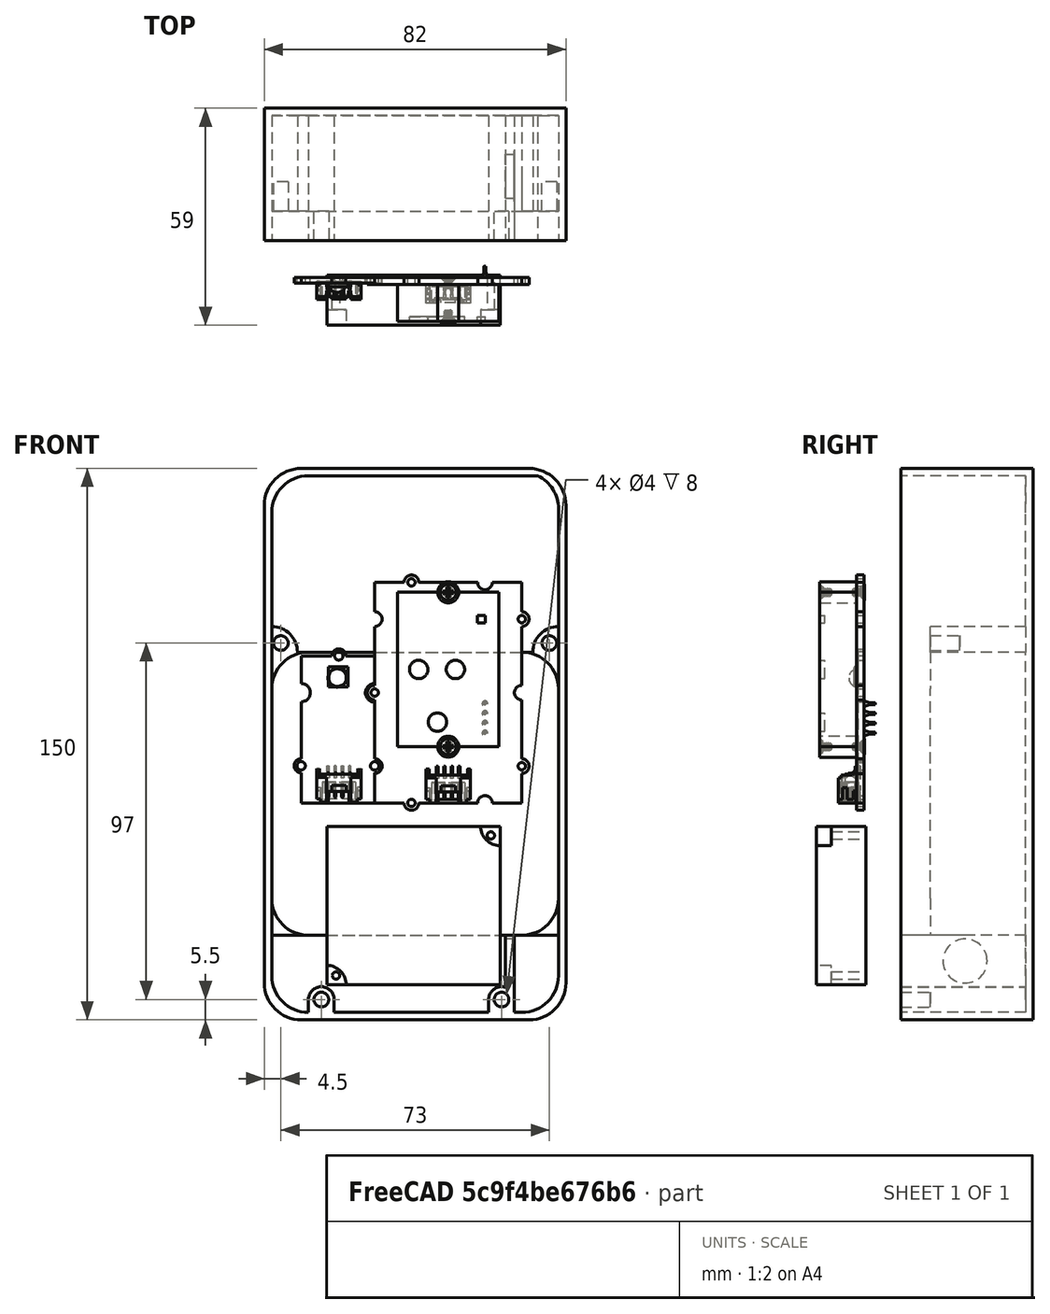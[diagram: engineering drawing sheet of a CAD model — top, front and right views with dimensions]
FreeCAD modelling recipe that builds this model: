
FCSTD DOCUMENT  (FreeCAD 0.20R29177 +233 (Git))
Label: wearableCad_09_10_2022
License: All rights reserved
LicenseURL: http://en.wikipedia.org/wiki/All_rights_reserved
objects: Part::Cylinder×30, Part::Box×23, Part::Cut×23, Part::MultiFuse×14, Part::Feature×3
note: 93 computed .brp shape members not serialized (recipe doc carries the construction recipe); baked Part::Feature solids carry a one-line shape summary decoded from their .brp

FEATURE [Part::Feature] Feature  label="Odroid-C4"
  Placement = pos=(66,-10,0) rot=(0.57735,-0.57735,0.57735;2.0944rad)
  shape: bbox 57.1 x 20.65 x 89.5 mm, 2775 faces, 0 solids (baked)
FEATURE [Part::Feature] Feature001  label="SCD30"
  Placement = pos=(-1.3e-14,-22,57) rot=(0,-1,0;1.5708rad)
  shape: bbox 44 x 15.1 x 64 mm, 422 faces, 13 solids (baked)
FEATURE [Part::Feature] Feature002  label="bme280"
  Placement = pos=(-60,-20,58) rot=(0.707107,0,0.707107;3.14159rad)
  shape: bbox 23.8 x 6.016 x 41.9 mm, 221 faces, 2 solids (baked)
FEATURE [Part::MultiFuse] Fusion  label="i2cSensors"
  Placement = pos=(68,0,0) rot=(0,0,1;0rad)
  Shapes = -> [Feature001,Feature002]
FEATURE [Part::Box] Box  label="ips7100"
  AttacherType = Attacher::AttachEngine3D
  Height = 43.1
  Length = 47.1
  Width = 13.55
FEATURE [Part::Cylinder] Cylinder
  Angle = 360
  AttacherType = Attacher::AttachEngine3D
  FirstAngle = 0
  Height = 13.55
  Placement = pos=(2.5,13.55,2.5) rot=(1,0,0;1.5708rad)
  Radius = 1
  SecondAngle = 0
FEATURE [Part::Cylinder] Cylinder001  label="semiCut"
  Angle = 90
  AttacherType = Attacher::AttachEngine3D
  FirstAngle = 0
  Height = 4.13
  Placement = pos=(0,4.13,-9e-16) rot=(1,0,0;1.5708rad)
  Radius = 5.25
  SecondAngle = 0
FEATURE [Part::MultiFuse] Fusion001  label="ipsCut"
  Shapes = -> [Cylinder,Cylinder001]
FEATURE [Part::Cylinder] Cylinder002
  Angle = 360
  AttacherType = Attacher::AttachEngine3D
  FirstAngle = 0
  Height = 13.55
  Placement = pos=(2.5,13.55,2.5) rot=(1,0,0;1.5708rad)
  Radius = 1
  SecondAngle = 0
FEATURE [Part::Cylinder] Cylinder003  label="semiCut001"
  Angle = 90
  AttacherType = Attacher::AttachEngine3D
  FirstAngle = 0
  Height = 4.13
  Placement = pos=(0,4.13,-9e-16) rot=(1,0,0;1.5708rad)
  Radius = 5.25
  SecondAngle = 0
FEATURE [Part::MultiFuse] Fusion002  label="ipsCut001"
  Placement = pos=(47.1,0,43.1) rot=(0,1,0;3.14159rad)
  Shapes = -> [Cylinder002,Cylinder003]
FEATURE [Part::MultiFuse] Fusion003
  Shapes = -> [Fusion001,Fusion002]
FEATURE [Part::Cut] Cut  label="ips7100V"
  Base = -> Box
  Placement = pos=(15,-33,7.55) rot=(0,0,1;0rad)
  Tool = -> Fusion003
FEATURE [Part::Box] Box001  label="V25B"
  AttacherType = Attacher::AttachEngine3D
  Height = 77
  Length = 78
  Width = 26
FEATURE [Part::Cylinder] Cylinder004
  Angle = 90
  AttacherType = Attacher::AttachEngine3D
  FirstAngle = 0
  Height = 26
  Placement = pos=(0,26,-5.8e-15) rot=(1,0,0;1.5708rad)
  Radius = 10
  SecondAngle = 0
FEATURE [Part::Box] Box002  label="Cube"
  AttacherType = Attacher::AttachEngine3D
  Height = 10
  Length = 10
  Width = 26
FEATURE [Part::Cut] Cut001
  Base = -> Box002
  Placement = pos=(68,0,67) rot=(0,0,1;0rad)
  Tool = -> Cylinder004
FEATURE [Part::Box] Box003  label="Cube001"
  AttacherType = Attacher::AttachEngine3D
  Height = 10
  Length = 10
  Width = 26
FEATURE [Part::Cylinder] Cylinder005
  Angle = 90
  AttacherType = Attacher::AttachEngine3D
  FirstAngle = 0
  Height = 26
  Placement = pos=(0,26,-5.8e-15) rot=(1,0,0;1.5708rad)
  Radius = 10
  SecondAngle = 0
FEATURE [Part::Cut] Cut002
  Base = -> Box003
  Placement = pos=(68,0,10) rot=(0,1,0;1.5708rad)
  Tool = -> Cylinder005
FEATURE [Part::Box] Box004  label="Cube002"
  AttacherType = Attacher::AttachEngine3D
  Height = 10
  Length = 10
  Width = 26
FEATURE [Part::Cylinder] Cylinder006
  Angle = 90
  AttacherType = Attacher::AttachEngine3D
  FirstAngle = 0
  Height = 26
  Placement = pos=(0,26,-5.8e-15) rot=(1,0,0;1.5708rad)
  Radius = 10
  SecondAngle = 0
FEATURE [Part::Cut] Cut003
  Base = -> Box004
  Placement = pos=(10,0,10) rot=(0,1,0;3.14159rad)
  Tool = -> Cylinder006
FEATURE [Part::Box] Box005  label="Cube003"
  AttacherType = Attacher::AttachEngine3D
  Height = 10
  Length = 10
  Width = 26
FEATURE [Part::Cylinder] Cylinder007
  Angle = 90
  AttacherType = Attacher::AttachEngine3D
  FirstAngle = 0
  Height = 26
  Placement = pos=(0,26,-5.8e-15) rot=(1,0,0;1.5708rad)
  Radius = 10
  SecondAngle = 0
FEATURE [Part::Cut] Cut004
  Base = -> Box005
  Placement = pos=(10,0,67) rot=(0,-1,0;1.5708rad)
  Tool = -> Cylinder007
FEATURE [Part::MultiFuse] Fusion004  label="v25Cuts"
  Shapes = -> [Cut001,Cut002,Cut003,Cut004]
FEATURE [Part::Cut] Cut005  label="V25B001"
  Base = -> Box001
  Placement = pos=(0,-2,21) rot=(0,0,1;0rad)
  Tool = -> Fusion004
FEATURE [Part::Box] Box007  label="Cube004"
  AttacherType = Attacher::AttachEngine3D
  Height = 10
  Length = 10
  Placement = pos=(0,-10,0) rot=(0,0,1;0rad)
  Width = 36
FEATURE [Part::Cylinder] Cylinder008
  Angle = 90
  AttacherType = Attacher::AttachEngine3D
  FirstAngle = 0
  Height = 36
  Placement = pos=(0,26,-5.8e-15) rot=(1,0,0;1.5708rad)
  Radius = 10
  SecondAngle = 0
FEATURE [Part::Cut] Cut006
  Base = -> Box007
  Placement = pos=(8,18,8) rot=(-0.707107,0,0.707107;3.14159rad)
  Tool = -> Cylinder008
FEATURE [Part::Box] Box008  label="baseOut001"
  AttacherType = Attacher::AttachEngine3D
  Height = 150
  Length = 82
  Placement = pos=(80,26,-2) rot=(0,0,1;3.14159rad)
  Width = 36
FEATURE [Part::Box] Box009  label="Cube005"
  AttacherType = Attacher::AttachEngine3D
  Height = 10
  Length = 10
  Placement = pos=(0,-10,0) rot=(0,0,1;0rad)
  Width = 36
FEATURE [Part::Cylinder] Cylinder009
  Angle = 90
  AttacherType = Attacher::AttachEngine3D
  FirstAngle = 0
  Height = 36
  Placement = pos=(0,26,-5.8e-15) rot=(1,0,0;1.5708rad)
  Radius = 10
  SecondAngle = 0
FEATURE [Part::Cut] Cut007
  Base = -> Box009
  Placement = pos=(70,18,8) rot=(1,0,0;3.14159rad)
  Tool = -> Cylinder009
FEATURE [Part::Box] Box010  label="Cube006"
  AttacherType = Attacher::AttachEngine3D
  Height = 10
  Length = 10
  Placement = pos=(0,-10,0) rot=(0,0,1;0rad)
  Width = 36
FEATURE [Part::Cylinder] Cylinder010
  Angle = 90
  AttacherType = Attacher::AttachEngine3D
  FirstAngle = 0
  Height = 36
  Placement = pos=(0,26,-5.8e-15) rot=(1,0,0;1.5708rad)
  Radius = 10
  SecondAngle = 0
FEATURE [Part::Cut] Cut008
  Base = -> Box010
  Placement = pos=(8,18,138) rot=(0,0,1;3.14159rad)
  Tool = -> Cylinder010
FEATURE [Part::Box] Box011  label="Cube007"
  AttacherType = Attacher::AttachEngine3D
  Height = 10
  Length = 10
  Placement = pos=(0,-10,0) rot=(0,0,1;0rad)
  Width = 36
FEATURE [Part::Cylinder] Cylinder011
  Angle = 90
  AttacherType = Attacher::AttachEngine3D
  FirstAngle = 0
  Height = 36
  Placement = pos=(0,26,-5.8e-15) rot=(1,0,0;1.5708rad)
  Radius = 10
  SecondAngle = 0
FEATURE [Part::Cut] Cut009
  Base = -> Box011
  Placement = pos=(70,18,138) rot=(0.707107,0,0.707107;3.14159rad)
  Tool = -> Cylinder011
FEATURE [Part::MultiFuse] Fusion005
  Placement = pos=(0,-2,0) rot=(0,0,1;0rad)
  Shapes = -> [Cut006,Cut007,Cut008,Cut009]
FEATURE [Part::Cut] Cut010  label="BaseOut"
  Base = -> Box008
  Tool = -> Fusion005
FEATURE [Part::Box] Box013  label="Cube009"
  AttacherType = Attacher::AttachEngine3D
  Height = 10
  Length = 10
  Placement = pos=(0,-8,0) rot=(0,0,1;0rad)
  Width = 34
FEATURE [Part::Box] Box014  label="baseOut002"
  AttacherType = Attacher::AttachEngine3D
  Height = 146
  Length = 78
  Placement = pos=(80,26,-2) rot=(0,0,1;3.14159rad)
  Width = 34
FEATURE [Part::Box] Box015  label="Cube010"
  AttacherType = Attacher::AttachEngine3D
  Height = 10
  Length = 10
  Placement = pos=(0,-8,0) rot=(0,0,1;0rad)
  Width = 34
FEATURE [Part::Box] Box016  label="Cube011"
  AttacherType = Attacher::AttachEngine3D
  Height = 10
  Length = 10
  Placement = pos=(0,-8,0) rot=(0,0,1;0rad)
  Width = 34
FEATURE [Part::Box] Box017  label="Cube012"
  AttacherType = Attacher::AttachEngine3D
  Height = 10
  Length = 10
  Placement = pos=(0,-8,0) rot=(0,0,1;0rad)
  Width = 34
FEATURE [Part::Cylinder] Cylinder013
  Angle = 90
  AttacherType = Attacher::AttachEngine3D
  FirstAngle = 0
  Height = 34
  Placement = pos=(0,26,-5.8e-15) rot=(1,0,0;1.5708rad)
  Radius = 10
  SecondAngle = 0
FEATURE [Part::Cut] Cut012
  Base = -> Box013
  Placement = pos=(12,18,8) rot=(0.707107,0,-0.707107;3.14159rad)
  Tool = -> Cylinder013
FEATURE [Part::Cylinder] Cylinder014
  Angle = 90
  AttacherType = Attacher::AttachEngine3D
  FirstAngle = 0
  Height = 34
  Placement = pos=(0,26,-5.8e-15) rot=(1,0,0;1.5708rad)
  Radius = 10
  SecondAngle = 0
FEATURE [Part::Cut] Cut013
  Base = -> Box015
  Placement = pos=(70,18,8) rot=(1,0,0;3.14159rad)
  Tool = -> Cylinder014
FEATURE [Part::Cylinder] Cylinder015
  Angle = 90
  AttacherType = Attacher::AttachEngine3D
  FirstAngle = 0
  Height = 34
  Placement = pos=(0,26,-5.8e-15) rot=(1,0,0;1.5708rad)
  Radius = 10
  SecondAngle = 0
FEATURE [Part::Cut] Cut014
  Base = -> Box016
  Placement = pos=(12,18,134) rot=(0,0,1;3.14159rad)
  Tool = -> Cylinder015
FEATURE [Part::Cylinder] Cylinder016
  Angle = 90
  AttacherType = Attacher::AttachEngine3D
  FirstAngle = 0
  Height = 34
  Placement = pos=(0,26,-5.8e-15) rot=(1,0,0;1.5708rad)
  Radius = 10
  SecondAngle = 0
FEATURE [Part::Cut] Cut015
  Base = -> Box017
  Placement = pos=(70,18,135) rot=(0.707107,0,0.707107;3.14159rad)
  Tool = -> Cylinder016
FEATURE [Part::MultiFuse] Fusion006
  Shapes = -> [Cut012,Cut013,Cut014,Cut015]
FEATURE [Part::Cut] Cut016  label="BaseOut001"
  Base = -> Box014
  Placement = pos=(-2,-2,2) rot=(0,0,1;0rad)
  Tool = -> Fusion006
FEATURE [Part::Cut] Cut017  label="baseOut"
  Base = -> Cut010
  Tool = -> Cut016
FEATURE [Part::Box] Box018  label="Cube013"
  AttacherType = Attacher::AttachEngine3D
  Height = 10
  Length = 10
  Placement = pos=(10,26,0) rot=(0,0,-1;3.14159rad)
  Width = 26
FEATURE [Part::Cylinder] Cylinder017
  Angle = 90
  AttacherType = Attacher::AttachEngine3D
  FirstAngle = 0
  Height = 26
  Placement = pos=(0,26,-5.8e-15) rot=(1,0,0;1.5708rad)
  Radius = 10
  SecondAngle = 0
FEATURE [Part::Cut] Cut018  label="batterySupport"
  Base = -> Box018
  Placement = pos=(10,-2,31) rot=(0,1,0;3.14159rad)
  Tool = -> Cylinder017
FEATURE [Part::Box] Box019  label="Cube014"
  AttacherType = Attacher::AttachEngine3D
  Height = 10
  Length = 10
  Placement = pos=(10,26,0) rot=(0,0,1;3.14159rad)
  Width = 26
FEATURE [Part::Cylinder] Cylinder018
  Angle = 90
  AttacherType = Attacher::AttachEngine3D
  FirstAngle = 0
  Height = 26
  Placement = pos=(0,26,-5.8e-15) rot=(1,0,0;1.5708rad)
  Radius = 10
  SecondAngle = 0
FEATURE [Part::Cut] Cut019  label="batterySupport001"
  Base = -> Box019
  Placement = pos=(68,-2,31) rot=(0,-1,0;4.71239rad)
  Tool = -> Cylinder018
FEATURE [Part::Box] Box020  label="Cube015"
  AttacherType = Attacher::AttachEngine3D
  Height = 10
  Length = 10
  Placement = pos=(10,26,0) rot=(0,0,1;3.14159rad)
  Width = 26
FEATURE [Part::Cylinder] Cylinder019
  Angle = 90
  AttacherType = Attacher::AttachEngine3D
  FirstAngle = 0
  Height = 26
  Placement = pos=(0,26,-5.8e-15) rot=(1,0,0;1.5708rad)
  Radius = 10
  SecondAngle = 0
FEATURE [Part::Cut] Cut020  label="batterySupport002"
  Base = -> Box020
  Placement = pos=(68,-2,88) rot=(0,0,1;0rad)
  Tool = -> Cylinder019
FEATURE [Part::Box] Box021  label="Cube016"
  AttacherType = Attacher::AttachEngine3D
  Height = 10
  Length = 10
  Placement = pos=(10,26,0) rot=(0,0,1;3.14159rad)
  Width = 26
FEATURE [Part::Cylinder] Cylinder020
  Angle = 90
  AttacherType = Attacher::AttachEngine3D
  FirstAngle = 0
  Height = 26
  Placement = pos=(0,26,-5.8e-15) rot=(1,0,0;1.5708rad)
  Radius = 10
  SecondAngle = 0
FEATURE [Part::Cut] Cut021  label="batterySupport003"
  Base = -> Box021
  Placement = pos=(10,-2,88) rot=(0,1,0;4.71239rad)
  Tool = -> Cylinder020
FEATURE [Part::Cylinder] Cylinder021
  Angle = 360
  AttacherType = Attacher::AttachEngine3D
  FirstAngle = 0
  Height = 34
  Placement = pos=(13.5,24,3.5) rot=(1,0,0;1.5708rad)
  Radius = 3.5
  SecondAngle = 0
FEATURE [Part::Cylinder] Cylinder022
  Angle = 360
  AttacherType = Attacher::AttachEngine3D
  FirstAngle = 0
  Height = 8
  Placement = pos=(13.5,-2,3.5) rot=(1,0,0;1.5708rad)
  Radius = 1.75
  SecondAngle = 0
FEATURE [Part::Box] Box022  label="Cube017"
  AttacherType = Attacher::AttachEngine3D
  Height = 3.5
  Length = 7
  Placement = pos=(10,24,3.5) rot=(1,0,0;3.14159rad)
  Width = 34
FEATURE [Part::Cylinder] Cylinder023
  Angle = 360
  AttacherType = Attacher::AttachEngine3D
  FirstAngle = 0
  Height = 34
  Placement = pos=(62.5,24,3.5) rot=(1,0,0;1.5708rad)
  Radius = 3.5
  SecondAngle = 0
FEATURE [Part::Cylinder] Cylinder024
  Angle = 360
  AttacherType = Attacher::AttachEngine3D
  FirstAngle = 0
  Height = 8
  Placement = pos=(62.5,-2,3.5) rot=(1,0,0;1.5708rad)
  Radius = 1.75
  SecondAngle = 0
FEATURE [Part::Box] Box023  label="Cube018"
  AttacherType = Attacher::AttachEngine3D
  Height = 3.5
  Length = 7
  Placement = pos=(59,24,3.5) rot=(1,0,0;3.14159rad)
  Width = 34
FEATURE [Part::Cylinder] Cylinder025
  Angle = 360
  AttacherType = Attacher::AttachEngine3D
  FirstAngle = 0
  Height = 20
  Radius = 6
  SecondAngle = 0
FEATURE [Part::Cylinder] Cylinder026
  Angle = 360
  AttacherType = Attacher::AttachEngine3D
  FirstAngle = 0
  Height = 5
  Radius = 7
  SecondAngle = 0
FEATURE [Part::MultiFuse] Fusion007  label="powerSwitch"
  Placement = pos=(71,7.5,14) rot=(0,1,0;4.71239rad)
  Shapes = -> [Cylinder025,Cylinder026]
FEATURE [Part::Box] Box024  label="Cube019"
  AttacherType = Attacher::AttachEngine3D
  Height = 17.5
  Length = 2.5
  Placement = pos=(63.5,24,21) rot=(1,0,0;3.14159rad)
  Width = 34
FEATURE [Part::MultiFuse] Fusion008  label="base"
  Shapes = -> [Cut017,Cut018,Cut019,Cut020,Cut021]
FEATURE [Part::MultiFuse] Fusion009  label="base001"
  Shapes = -> [Cylinder021,Cylinder023,Box022,Box023,Box024,Fusion008]
FEATURE [Part::MultiFuse] Fusion010  label="baseCuts"
  Shapes = -> [Cylinder024,Cylinder022,Fusion007]
FEATURE [Part::Cut] Cut022  label="base002"
  Base = -> Fusion009
  Tool = -> Fusion010
FEATURE [Part::Cylinder] Cylinder027  label="mainMounts"
  Angle = 90
  AttacherType = Attacher::AttachEngine3D
  FirstAngle = 0
  Height = 26
  Placement = pos=(0,24,98) rot=(1,0,0;1.5708rad)
  Radius = 7
  SecondAngle = 0
FEATURE [Part::Cylinder] Cylinder028  label="mainMounts001"
  Angle = 90
  AttacherType = Attacher::AttachEngine3D
  FirstAngle = 0
  Height = 26
  Placement = pos=(78,24,98) rot=(0.57735,-0.57735,0.57735;2.0944rad)
  Radius = 7
  SecondAngle = 0
FEATURE [Part::Cylinder] Cylinder029
  Angle = 360
  AttacherType = Attacher::AttachEngine3D
  FirstAngle = 0
  Height = 8
  Placement = pos=(2.5,-2,100.5) rot=(1,0,0;1.5708rad)
  Radius = 1.75
  SecondAngle = 0
FEATURE [Part::Cylinder] Cylinder030
  Angle = 360
  AttacherType = Attacher::AttachEngine3D
  FirstAngle = 0
  Height = 8
  Placement = pos=(75.5,-2,100.5) rot=(1,0,0;1.5708rad)
  Radius = 1.75
  SecondAngle = 0
FEATURE [Part::MultiFuse] Fusion011  label="baseCuts001"
  Placement = pos=(0,8,0) rot=(0,0,1;0rad)
  Shapes = -> [Cylinder029,Cylinder030]
FEATURE [Part::MultiFuse] Fusion012
  Shapes = -> [Cylinder028,Cylinder027]
FEATURE [Part::MultiFuse] Fusion013  label="base003"
  Shapes = -> [Cut022,Fusion012]
FEATURE [Part::Cut] Cut023  label="base004"
  Base = -> Fusion013
  Tool = -> Fusion011
